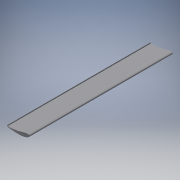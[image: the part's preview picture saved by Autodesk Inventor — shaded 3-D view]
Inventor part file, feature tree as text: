
AUTODESK INVENTOR PART (.ipt)
format: ipt  version: 2018.2 (Build 222227000, 227)  size: 162,816 bytes
history: native  units: mm
features: other x4, extrude x2, sketch x2, mirror x1, projected_geometry x1
ambient origin geometry x8: Origin, YZ Plane, XZ Plane, XY Plane, X Axis, Y Axis, Z Axis, Center Point
bodies: Body1 (feature_tree)
feature tree (10):
  other  "main frap.ipt"
  extrude  "押し出し2"  Depth=4.0mm
  mirror  "ミラー2"
  extrude  "押し出し3"  Depth=304.0mm TaperAngle=0.0deg
  other  "ソリッド1::main frap.ipt"
  other  "TaggingFeature1"
  sketch  "スケッチ2"
  projected_geometry  "投影ループ2"
  sketch  "スケッチ3"
  other  "ソリッド1"
